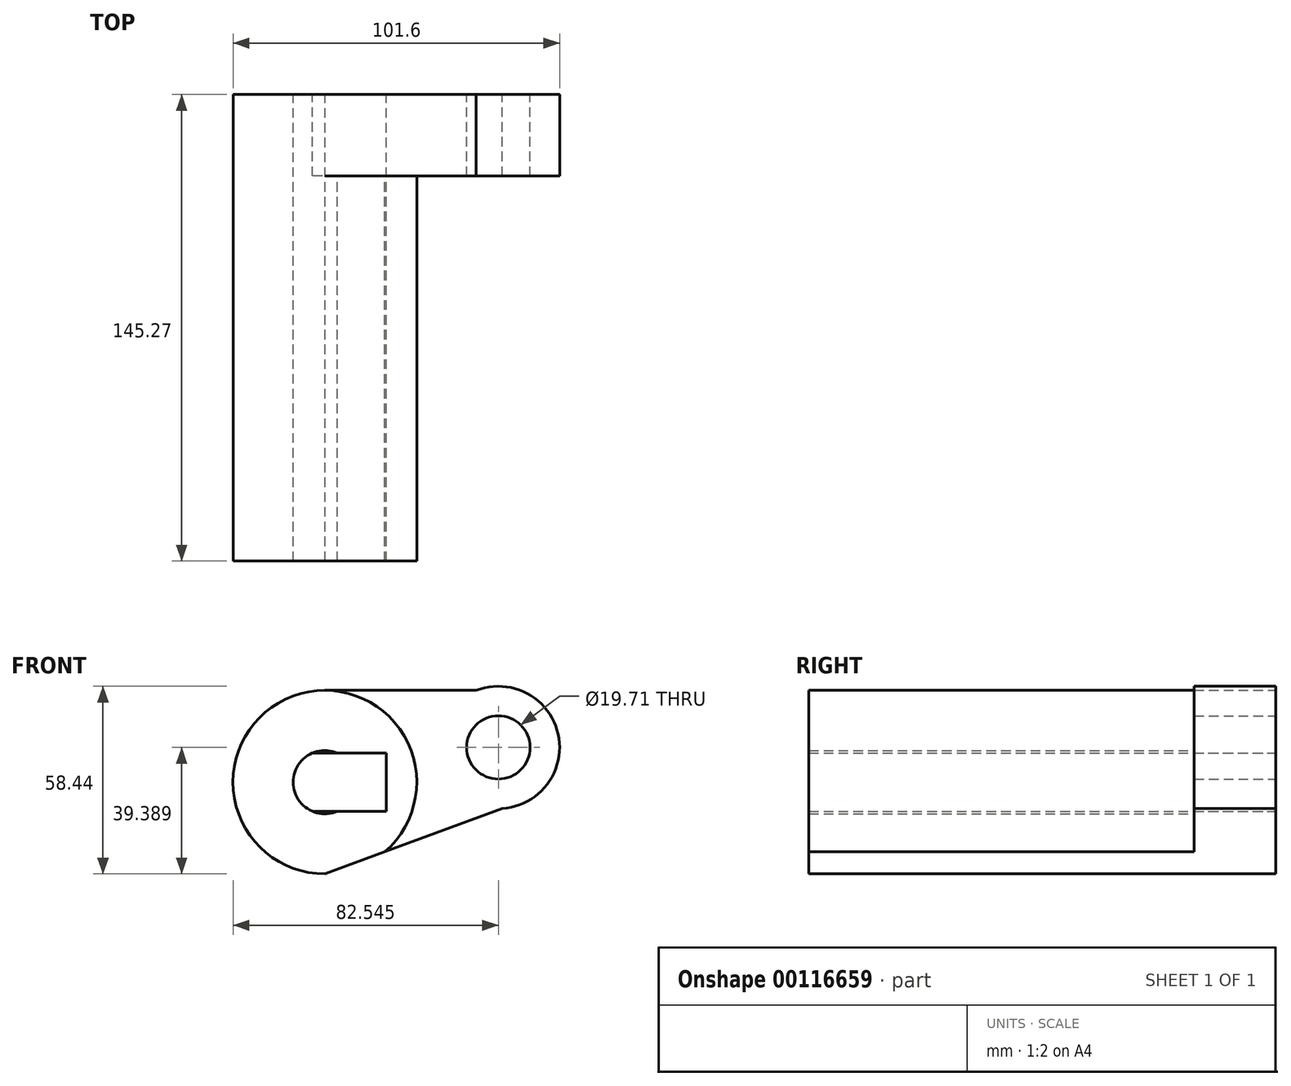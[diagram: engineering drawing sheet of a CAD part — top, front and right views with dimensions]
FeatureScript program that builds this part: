
annotation { "Feature Type Name" : "Feature", "Feature Type Description" : "" }
export const myFeature = defineFeature(function(context is Context, id is Id, definition is map)
    precondition{}
    {
        {
            var Q0;
            Q0=qCreatedBy(makeId("Front.planeOp"),FACE);
            var sketch = newSketch(context, id + "F0", { "sketchPlane" : qUnion([Q0])});
            skCircle(sketch, "E0", {"center": v(0, 0) * mm, "radius": 28.58 * mm});
            skCircle(sketch, "E1", {"center": v(53.98, 10.82) * mm, "radius": 19.05 * mm});
            skLineSegment(sketch, "E2", {"start": v(0, 28.58) * mm, "end": v(47.07, 28.58) * mm});
            skLineSegment(sketch, "E3", {"start": v(0, -28.58) * mm, "end": v(55.19, -8.2) * mm});
            skCircle(sketch, "E4", {"center": v(0, 0) * mm, "radius": 9.86 * mm});
            skCircle(sketch, "E5", {"center": v(53.98, 10.82) * mm, "radius": 9.86 * mm});
            skLineSegment(sketch, "E6.bottom", {"start": v(19.05, -9.06) * mm, "end": v(-19.05, -9.06) * mm});
            skLineSegment(sketch, "E6.top", {"start": v(19.05, 9.06) * mm, "end": v(-19.05, 9.06) * mm});
            skLineSegment(sketch, "E6.left", {"start": v(19.05, -9.06) * mm, "end": v(19.05, 9.06) * mm});
            skLineSegment(sketch, "E6.right", {"start": v(-19.05, -9.06) * mm, "end": v(-19.05, 9.06) * mm});
            skSolve(sketch);
        }
        {
            var Q0;
            {var subQ0=sQuery(id+"F0.wireOp",EDGE,"E3");var subQ1=sQuery(id+"F0.wireOp",EDGE,"E0");var subQ2=makeQuery(id+"F0.imprint","INTERSECT",VERTEX,{"disambiguationData":[OD(0.0)],"derivedFrom":[subQ1,subQ0]});Q0=makeQuery(id+"F0.imprint","IMPRINT",FACE,{"disambiguationData":[TD([[makeQuery(id+"F0.imprint","IMPRINT",EDGE,{"disambiguationData":[TD([[subQ2,-1.0]])],"derivedFrom":subQ1}),1.0]])]});}
            var Q1;
            {var subQ0=sQuery(id+"F0.wireOp",EDGE,"E2");Q1=makeQuery(id+"F0.imprint","IMPRINT",FACE,{"disambiguationData":[TD([[makeQuery(id+"F0.imprint","IMPRINT",EDGE,{"derivedFrom":subQ0}),-1.0]])]});}
            var Q2;
            Q2=makeQuery(id+"F0.imprint","IMPRINT",FACE,{"disambiguationData":[TD([[makeQuery(id+"F0.imprint","IMPRINT",EDGE,{"derivedFrom":sQuery(id+"F0.wireOp",EDGE,"E5")}),-1.0]])]});
            var Q3;
            {var subQ0=sQuery(id+"F0.wireOp",EDGE,"E6.left");Q3=makeQuery(id+"F0.imprint","IMPRINT",FACE,{"disambiguationData":[TD([[makeQuery(id+"F0.imprint","IMPRINT",EDGE,{"derivedFrom":subQ0}),-1.0]])]});}
            var Q4;
            {var subQ5=sQuery(id+"F0.wireOp",EDGE,"E6.right");Q4=makeQuery(id+"F0.imprint","IMPRINT",FACE,{"disambiguationData":[TD([[makeQuery(id+"F0.imprint","IMPRINT",EDGE,{"derivedFrom":subQ5}),-1.0]])]});}
            var Q5;
            {var subQ0=sQuery(id+"F0.wireOp",EDGE,"E6.top");var subQ1=sQuery(id+"F0.wireOp",EDGE,"E4");var subQ2=makeQuery(id+"F0.imprint","INTERSECT",VERTEX,{"disambiguationData":[OD(0.0)],"derivedFrom":[subQ1,subQ0]});Q5=makeQuery(id+"F0.imprint","IMPRINT",FACE,{"disambiguationData":[TD([[makeQuery(id+"F0.imprint","IMPRINT",EDGE,{"disambiguationData":[TD([[subQ2,1.0]])],"derivedFrom":subQ1}),1.0]])]});}
            var Q6;
            {var subQ0=sQuery(id+"F0.wireOp",EDGE,"E6.bottom");var subQ1=sQuery(id+"F0.wireOp",EDGE,"E4");var subQ2=makeQuery(id+"F0.imprint","INTERSECT",VERTEX,{"disambiguationData":[OD(0.0)],"derivedFrom":[subQ1,subQ0]});Q6=makeQuery(id+"F0.imprint","IMPRINT",FACE,{"disambiguationData":[TD([[makeQuery(id+"F0.imprint","IMPRINT",EDGE,{"disambiguationData":[TD([[subQ2,-1.0]])],"derivedFrom":subQ1}),1.0]])]});}
            extrude(context, id + "F1", {"entities" : qUnion([Q0, Q1, Q2, Q3, Q4, Q5, Q6]), "depth" : 25.4 * mm});
        }
        {
            var Q0;
            {var subQ5=sQuery(id+"F0.wireOp",EDGE,"E6.right");Q0=makeQuery(id+"F0.imprint","IMPRINT",FACE,{"disambiguationData":[TD([[makeQuery(id+"F0.imprint","IMPRINT",EDGE,{"derivedFrom":subQ5}),-1.0]])]});}
            var Q1;
            {var subQ0=sQuery(id+"F0.wireOp",EDGE,"E6.left");Q1=makeQuery(id+"F0.imprint","IMPRINT",FACE,{"disambiguationData":[TD([[makeQuery(id+"F0.imprint","IMPRINT",EDGE,{"derivedFrom":subQ0}),-1.0]])]});}
            extrude(context, id + "F2", {"entities" : qUnion([Q0, Q1]), "operationType" : NewBodyOperationType.ADD, "depth" : 145.27 * mm});
        }
    });
